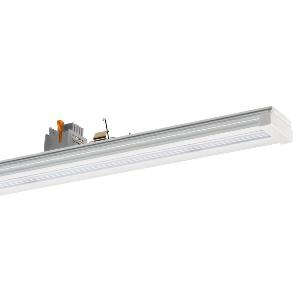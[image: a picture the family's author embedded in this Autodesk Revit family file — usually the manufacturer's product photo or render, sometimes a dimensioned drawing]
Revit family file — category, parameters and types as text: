
# Revit family: conveo_-_cvg_8000_850_w-p_da_7_226848049-00804940_332c
name_source: partatom
category: Lighting Fixtures
units: mm (PartAtom-declared; Revit-internal decimal feet)

## family parameters
Cut with Voids When Loaded = No
Host = Face
Light Source = No
Part Type = Normal
Room Calculation Point = No
Round Connector Dimension = Use Diameter
Shared = No

## types (1)
- CONVEO - CVG 8000/850/W-P/DA/7 (1 x LED, 8300 lm, 5000K)
    Apparent Load = 55 VA
    Approval mark = CE
    CIE Flux Codes = 54 85 97 100 100
    Color Rendering = 80-89
    Color Temperature = 5000K
    Control Gear = Electronic ballast
    Default Elevation = 1800 mm
    Description = CVG 8000/850/W-P/DA/7|Continuous-row system|light source: LED|work equipment: Adjustable electronic ballast, digital DALI|connected load: 220-240 V, 50-60 Hz|Power consumption: approx. 55 W|luminous flux: 8300 lm|luminous efficacy: 150 lm/W|colour temperature: Cold white, ca. 5000 K|color rendering index (CRI): >= 80|chromaticity tolerance:  3 SDCM|System of protection: IP 54|class of protection: I|technology: Continuously dimmable|luminaire body|material: Aluminium|surface: Powder coatet|colour: White|lamp cover: Acrylic (PMMA), Satine|weight (net): approx. 1.9 kg|Fastening: Available separately|minimum ambient temperature: -25 ░C|maximum ambient temperature: 45 ░C|glare control: Prism optics (linear)|Approval mark: VDE - ENEC|
    Frequency = 50 Hz
    Height = 70 mm
    Lamp = 1 x LED
    Lamp Light Flux = 8300 lm
    Lamp count = 1
    Length = 1500 mm
    Luminous efficacy = 151 lm/W
    Manufacturer = Waldmann
    ModVariant = No
    Model = 226848049-00804940
    Mounting Place = Ceiling
    Mounting Type = Pendant
    Number of Poles = 1
    OnlyDefault = Yes
    Power Factor = 1
    Product Name = CONVEO - CVG 8000/850/W-P/DA/7
    Product group = Continuous-row system (industry)
    ProductGroupID = 301
    Protection Class = Protection class I
    Protection Degree = IP 54
    RLX_Detail_Level = 1
    RlxData = <blob elided: 98853 chars, md5=8864bf3e>
    Socket = socket
    Standby Power = 0 W
    System Light Flux = 8300 lm
    System Power = 55 W
    Type Comments = Product without accessories
    Type Image = 226848019-00804937-1p7.jpg
    URL = http://relux.com
    VarID = ---
    Voltage = 230 V
    Voltage Range = 220-240 V
    Weight = 0.00 kg
    Width = 64 mm

## geometry (parser evidence)
native form markers: Blend x4, Sweep x10
no freeform markers — native parametric forms only
